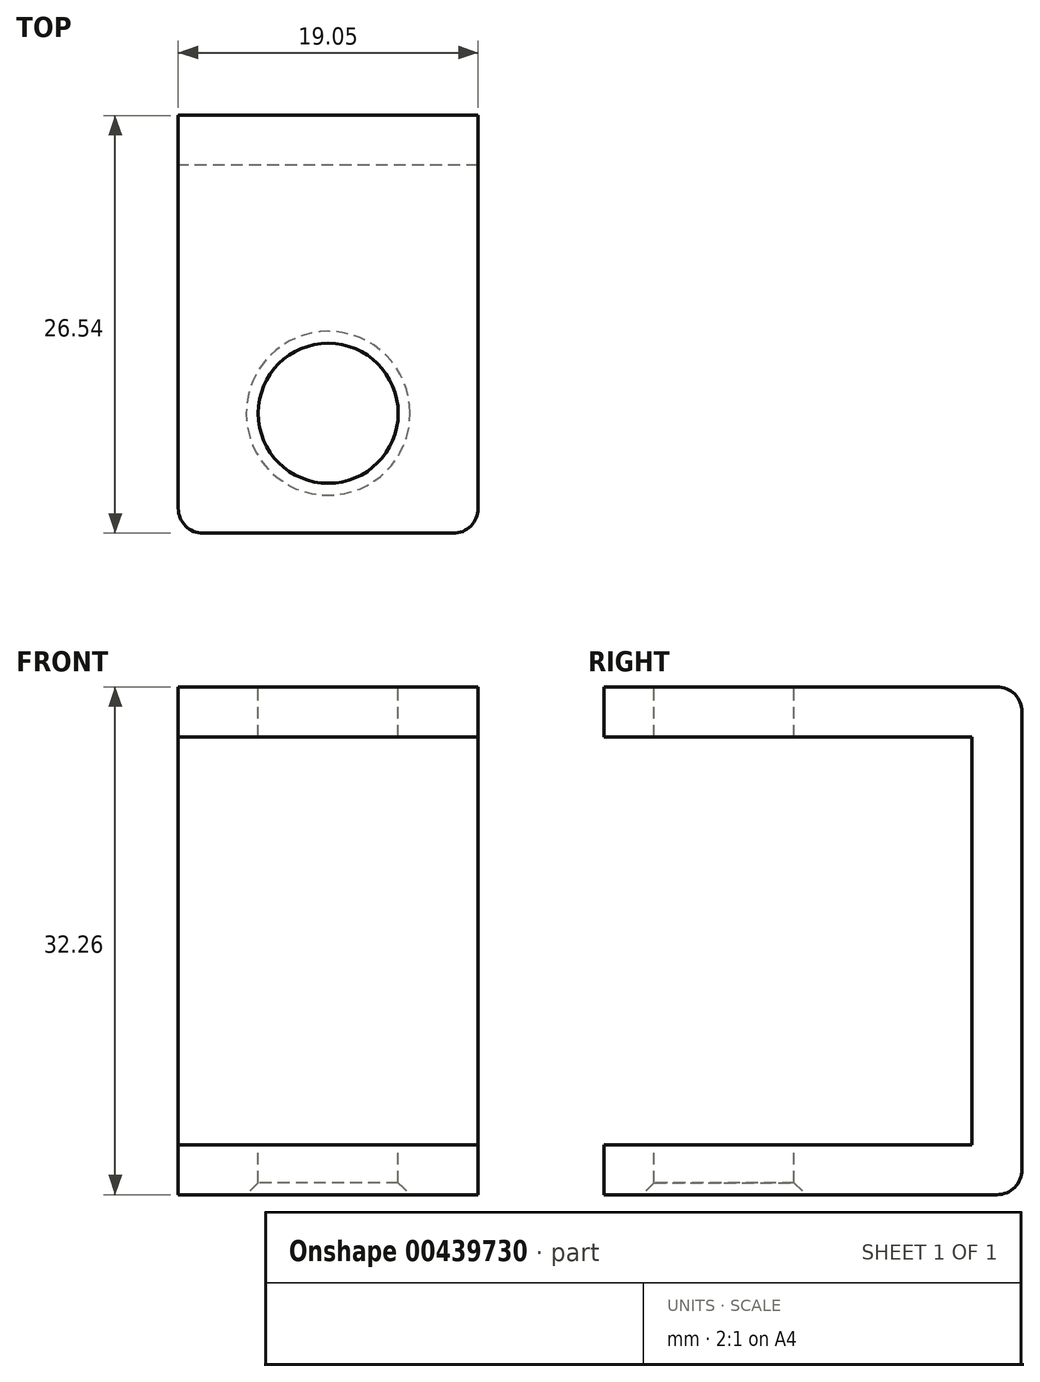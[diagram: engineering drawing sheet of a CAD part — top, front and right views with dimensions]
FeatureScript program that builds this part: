
annotation { "Feature Type Name" : "Feature", "Feature Type Description" : "" }
export const myFeature = defineFeature(function(context is Context, id is Id, definition is map)
    precondition{}
    {
        {
            var Q0;
            Q0=qCreatedBy(makeId("Right.planeOp"),FACE);
            var sketch = newSketch(context, id + "F0", { "sketchPlane" : qUnion([Q0])});
            skLineSegment(sketch, "E0.bottom", {"start": v(0, 0) * mm, "end": v(26.54, 0) * mm});
            skLineSegment(sketch, "E0.top", {"start": v(0, 3.18) * mm, "end": v(23.37, 3.18) * mm});
            skLineSegment(sketch, "E0.left", {"start": v(0, 0) * mm, "end": v(0, 3.18) * mm});
            skLineSegment(sketch, "E1.bottom", {"start": v(0, 32.26) * mm, "end": v(26.54, 32.26) * mm});
            skLineSegment(sketch, "E1.top", {"start": v(0, 29.08) * mm, "end": v(23.37, 29.08) * mm});
            skLineSegment(sketch, "E2", {"start": v(0, 32.26) * mm, "end": v(0, 29.08) * mm});
            skLineSegment(sketch, "E3", {"start": v(23.37, 3.18) * mm, "end": v(23.37, 29.08) * mm});
            skLineSegment(sketch, "E4", {"start": v(26.54, 0) * mm, "end": v(26.54, 32.26) * mm});
            skLineSegment(sketch, "E5", {"start": v(23.37, 29.08) * mm, "end": v(26.54, 29.08) * mm, "construction": true});
            skLineSegment(sketch, "E6", {"start": v(3.18, 21.78) * mm, "end": v(15.37, 21.78) * mm, "construction": true});
            skSolve(sketch);
        }
        {
            var Q0;
            Q0=qSketchRegion(id+"F0",true);
            extrude(context, id + "F1", {"entities" : qUnion([Q0]), "depth" : 19.05 * mm});
        }
        {
            var Q0;
            Q0=makeQuery(id+"F1.opExtrude","SWEPT_FACE",FACE,{"disambiguationData":[OSD([sQuery(id+"F0.wireOp",EDGE,"E0.top")])]});
            var sketch = newSketch(context, id + "F2", { "sketchPlane" : qUnion([Q0])});
            skCircle(sketch, "E7", {"center": v(9.53, 7.62) * mm, "radius": 4.45 * mm});
            skLineSegment(sketch, "E8", {"start": v(9.53, 0) * mm, "end": v(9.53, 7.62) * mm, "construction": true});
            skPoint(sketch, "E9.orphan", {"position": v(19.05, 11.68) * mm});
            skPoint(sketch, "E10", {"position": v(9.53, 3.18) * mm});
            skSolve(sketch);
        }
        {
            var Q0;
            Q0=qSketchRegion(id+"F2",true);
            extrude(context, id + "F3", {"entities" : qUnion([Q0]), "operationType" : NewBodyOperationType.REMOVE, "oppositeDirection" : true, "depth" : 25.4 * mm});
        }
        {
            var Q0;
            Q0=makeQuery(id+"F1.opExtrude","SWEPT_FACE",FACE,{"disambiguationData":[OSD([sQuery(id+"F0.wireOp",EDGE,"E1.bottom")])]});
            var sketch = newSketch(context, id + "F4", { "sketchPlane" : qUnion([Q0])});
            skCircle(sketch, "E11", {"center": v(9.53, 7.62) * mm, "radius": 4.45 * mm});
            skLineSegment(sketch, "E12", {"start": v(9.53, 7.62) * mm, "end": v(9.53, 0) * mm, "construction": true});
            skSolve(sketch);
        }
        {
            var Q0;
            Q0=qSketchRegion(id+"F4",true);
            extrude(context, id + "F5", {"entities" : qUnion([Q0]), "operationType" : NewBodyOperationType.REMOVE, "endBound" : BoundingType.UP_TO_NEXT, "oppositeDirection" : true, "depth" : 25.4 * mm});
        }
        {
            var Q0;
            Q0=makeQuery(id+"F1.opExtrude","CAP_EDGE",EDGE,{"disambiguationData":[OSD([sQuery(id+"F0.wireOp",EDGE,"E2")])],"isStart":false});
            var Q1;
            Q1=makeQuery(id+"F1.opExtrude","CAP_EDGE",EDGE,{"disambiguationData":[OSD([sQuery(id+"F0.wireOp",EDGE,"E2")])],"isStart":true});
            var Q2;
            Q2=makeQuery(id+"F1.opExtrude","CAP_EDGE",EDGE,{"disambiguationData":[OSD([sQuery(id+"F0.wireOp",EDGE,"E0.left")])],"isStart":true});
            var Q3;
            Q3=makeQuery(id+"F1.opExtrude","CAP_EDGE",EDGE,{"disambiguationData":[OSD([sQuery(id+"F0.wireOp",EDGE,"E0.left")])],"isStart":false});
            var Q4;
            Q4=makeQuery(id+"F1.opExtrude","SWEPT_EDGE",EDGE,{"disambiguationData":[OSD([sQuery(id+"F0.wireOp",EDGE,"E1.bottom"),sQuery(id+"F0.wireOp",EDGE,"E4")])]});
            var Q5;
            Q5=makeQuery(id+"F1.opExtrude","SWEPT_EDGE",EDGE,{"disambiguationData":[OSD([sQuery(id+"F0.wireOp",EDGE,"E0.bottom"),sQuery(id+"F0.wireOp",EDGE,"E4")])]});
            fillet(context, id + "F6", {"entities" : qUnion([Q0, Q1, Q2, Q3, Q4, Q5]), "radius" : 1.59 * mm, "tangentPropagation" : true, "allowEdgeOverflow" : false});
        }
        {
            var Q0;
            Q0=makeQuery(id+"F3.boolean.opBoolean","INTERSECT",EDGE,{"derivedFrom":[makeQuery(id+"F1.opExtrude","SWEPT_FACE",FACE,{"disambiguationData":[OSD([sQuery(id+"F0.wireOp",EDGE,"E0.bottom")])]}),makeQuery(id+"F3.opExtrude","SWEPT_FACE",FACE,{"disambiguationData":[OSD([sQuery(id+"F2.wireOp",EDGE,"E7")])]})]});
            var Q1;
            Q1=makeQuery(id+"F5.boolean.opBoolean","COPY",EDGE,{"derivedFrom":makeQuery(id+"F5.opExtrude","CAP_EDGE",EDGE,{"disambiguationData":[OSD([sQuery(id+"F4.wireOp",EDGE,"E11")])],"isStart":false})});
            var Q2;
            Q2=makeQuery(id+"F5.boolean.opBoolean","COPY",EDGE,{"derivedFrom":makeQuery(id+"F5.opExtrude","CAP_EDGE",EDGE,{"disambiguationData":[OSD([sQuery(id+"F4.wireOp",EDGE,"E11")])],"isStart":true})});
            var Q3;
            Q3=makeQuery(id+"F3.boolean.opBoolean","COPY",EDGE,{"derivedFrom":makeQuery(id+"F3.opExtrude","CAP_EDGE",EDGE,{"disambiguationData":[OSD([sQuery(id+"F2.wireOp",EDGE,"E7")])],"isStart":true})});
            chamfer(context, id + "F7", {"entities" : qUnion([Q0, Q1, Q2, Q3]), "width" : 0.76 * mm, "tangentPropagation" : true});
        }
    });
